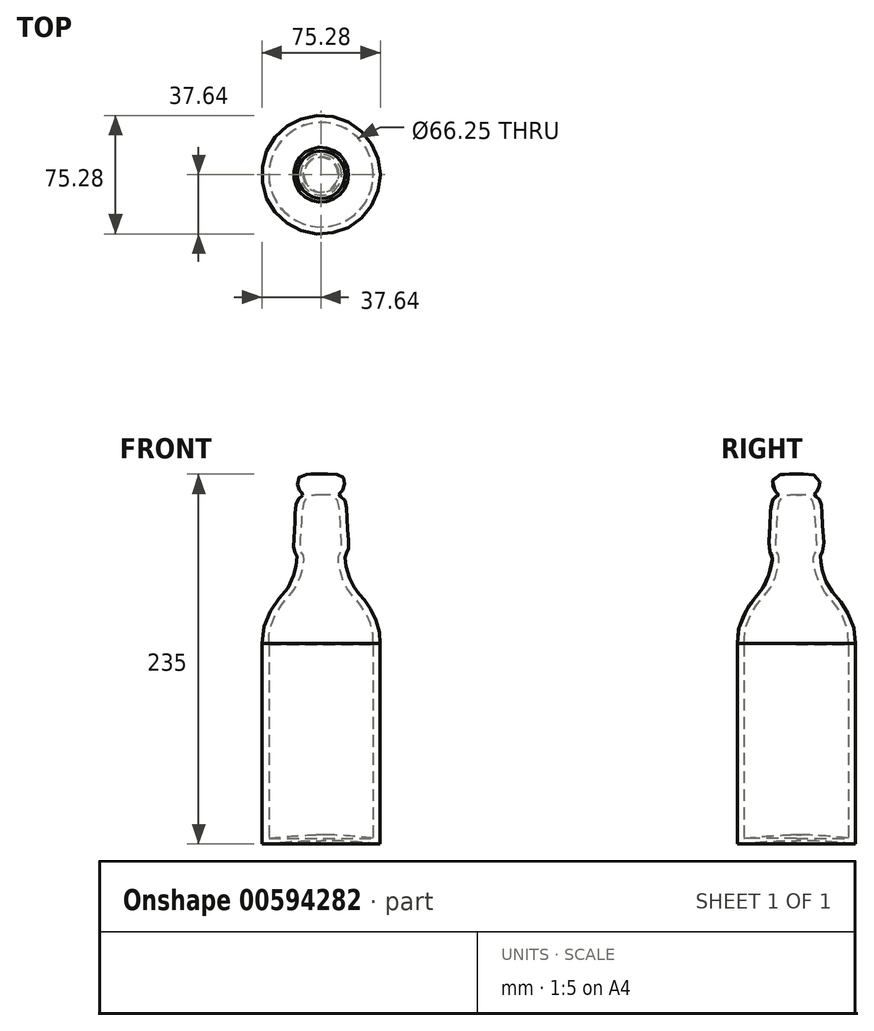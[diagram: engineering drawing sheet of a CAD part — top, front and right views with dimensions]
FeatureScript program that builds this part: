
annotation { "Feature Type Name" : "Feature", "Feature Type Description" : "" }
export const myFeature = defineFeature(function(context is Context, id is Id, definition is map)
    precondition{}
    {
        {
            var Q0;
            Q0=qCreatedBy(makeId("Front.planeOp"),FACE);
            var sketch = newSketch(context, id + "F0", { "sketchPlane" : qUnion([Q0])});
            skLineSegment(sketch, "E0", {"start": v(0, 0) * mm, "end": v(0, 234.95) * mm});
            skPoint(sketch, "E1", {"position": v(0, -29.78) * mm});
            skLineSegment(sketch, "E2", {"start": v(0, 0) * mm, "end": v(37.5, 0) * mm});
            skLineSegment(sketch, "E3", {"start": v(37.5, 0) * mm, "end": v(37.5, 127.36) * mm});
            skFitSpline(sketch, "E4", {"points": [v(37.5, 127.36) * mm, v(28.96, 153.05) * mm, v(19.93, 164.66) * mm, v(15.42, 183.36) * mm, v(17.02, 186.18) * mm, v(16.64, 203.22) * mm, v(14.55, 219.08) * mm, v(11.44, 221.88) * mm, v(13.34, 224.38) * mm, v(14.5, 232.32) * mm, v(0, 234.95) * mm], "startDerivative": vector(20.68, 149.5) * mm, "endDerivative": vector(-177.68, -3.37) * mm});
            skLineSegment(sketch, "E5", {"start": v(33.13, 3.68) * mm, "end": v(33.13, 126.77) * mm});
            skFitSpline(sketch, "E6", {"points": [v(33.13, 126.77) * mm, v(24.58, 152.47) * mm, v(15.55, 164.07) * mm, v(11.04, 182.77) * mm, v(12.64, 185.6) * mm, v(12.26, 202.63) * mm, v(10.18, 218.5) * mm, v(7.06, 221.3) * mm, v(0, 221.77) * mm], "startDerivative": vector(20.68, 149.5) * mm, "endDerivative": vector(-177.68, -3.37) * mm});
            skFitSpline(sketch, "E7", {"points": [v(33.13, 3.68) * mm, v(16.02, 5.25) * mm, v(0, 5.77) * mm], "startDerivative": vector(-33.88, 3.96) * mm, "endDerivative": vector(-32.36, -1.18) * mm});
            skFitSpline(sketch, "E8", {"points": [v(37.5, 0) * mm, v(16.02, 1.76) * mm, v(0, 2.09) * mm], "startDerivative": vector(-41.45, 3.96) * mm, "endDerivative": vector(-33.36, 0.13) * mm});
            skSolve(sketch);
        }
        {
            var Q0;
            Q0=makeQuery(id+"F0.imprint","IMPRINT",FACE,{"disambiguationData":[TD([[makeQuery(id+"F0.imprint","IMPRINT",EDGE,{"derivedFrom":sQuery(id+"F0.wireOp",EDGE,"E3")}),1.0]])]});
            var Q1;
            Q1=sQuery(id+"F0.wireOp",EDGE,"E0");
            revolve(context, id + "F1", {"entities" : qUnion([Q0]), "axis" : qUnion([Q1]), "revolveType" : RevolveType.FULL});
        }
    });
